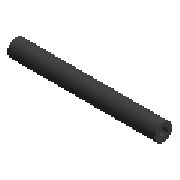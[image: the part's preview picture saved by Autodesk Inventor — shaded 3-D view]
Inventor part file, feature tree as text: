
AUTODESK INVENTOR PART (.ipt)
format: ipt  version: 2019 (Build 230136000, 136)  size: 305,664 bytes
history: native  units: mm (DEFAULTED — no unit token found)
features: other x3, sketch x2, plane x1, sweep x1
ambient origin geometry x8: Origin, YZ Plane, XZ Plane, XY Plane, X Axis, Y Axis, Z Axis, Center Point
bodies: Body1 (feature_tree)
feature tree (7):
  sketch  "Boceto 3D1"  dims[d4=-10.0mm d5=10.0mm]
  other  "Punto de trabajo3"
  other  "Punto de trabajo4"
  plane  "Plano de trabajo1"
  sketch  "Boceto2"  dims[d6=0.0mm d7=0.0mm]
  other  "Punto de trabajo5"
  sweep  "Barrido1"
